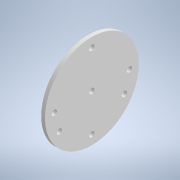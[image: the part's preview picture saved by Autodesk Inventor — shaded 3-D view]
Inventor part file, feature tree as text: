
AUTODESK INVENTOR PART (.ipt)
format: ipt  version: 2021 (Build 250183000, 183)  size: 112,128 bytes
history: native  units: mm
features: extrude x2, sketch x2
ambient origin geometry x8: Origin, YZ Plane, XZ Plane, XY Plane, X Axis, Y Axis, Z Axis, Center Point
bodies: Solid1 (feature_tree)
feature tree (4):
  extrude  "Extrusion1"  Depth=5.0mm TaperAngle=0.0deg
  extrude  "Extrusion2"  TaperAngle=0.0deg  [1 undecoded]
  sketch  "Sketch1"  dims[d0=125.0mm d1=5.0mm d2=0.0mm]
  sketch  "Sketch2"  dims[d3=7.0mm d4=0.0mm d5=50.0mm d6=40.0mm d8=360.0deg d10=30.0mm d12=360.0deg d14=0.0mm d15=0.0mm d16=7.0mm]
note: 1 required parameter value undecoded (feature->parameter linkage not recoverable at this tier; creation-order binding heuristic only, values carry confidence <= 0.55)
